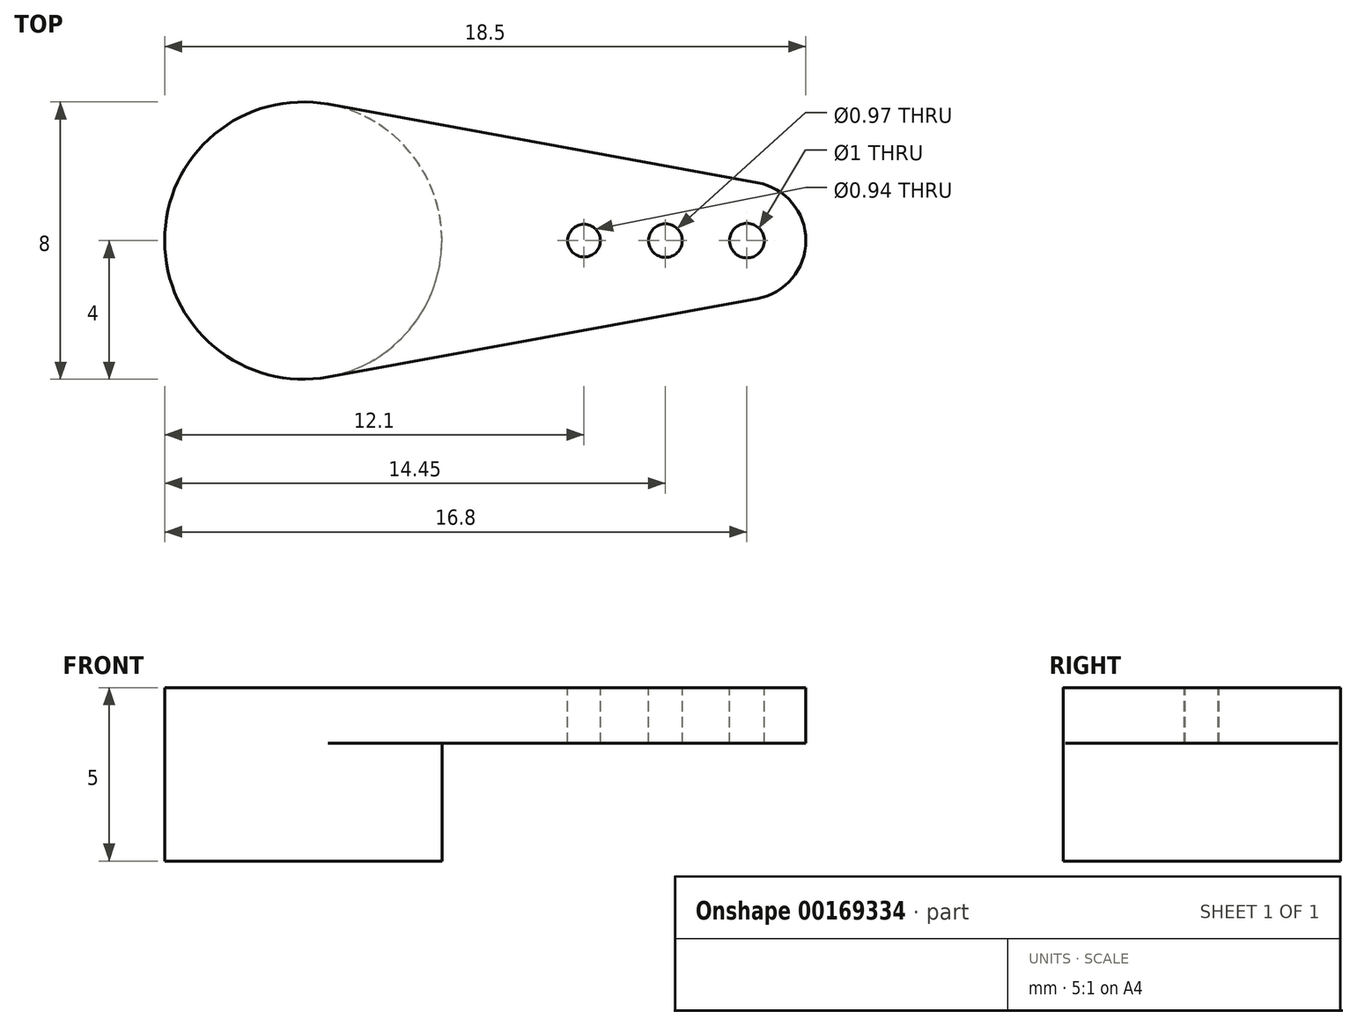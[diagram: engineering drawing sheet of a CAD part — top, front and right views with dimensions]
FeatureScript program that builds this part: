
annotation { "Feature Type Name" : "Feature", "Feature Type Description" : "" }
export const myFeature = defineFeature(function(context is Context, id is Id, definition is map)
    precondition{}
    {
        {
            var Q0;
            Q0=qCreatedBy(makeId("Front.planeOp"),FACE);
            var sketch = newSketch(context, id + "F0", { "sketchPlane" : qUnion([Q0])});
            skLineSegment(sketch, "E0.bottom", {"start": v(0, 0) * mm, "end": v(4, 0) * mm});
            skLineSegment(sketch, "E0.top", {"start": v(0, 3.4) * mm, "end": v(4, 3.4) * mm});
            skLineSegment(sketch, "E0.left", {"start": v(0, 0) * mm, "end": v(0, 3.4) * mm});
            skLineSegment(sketch, "E0.right", {"start": v(4, 0) * mm, "end": v(4, 3.4) * mm});
            skLineSegment(sketch, "E1.bottom", {"start": v(-4, 3.4) * mm, "end": v(14.5, 3.4) * mm});
            skLineSegment(sketch, "E1.top", {"start": v(-4, 5) * mm, "end": v(14.5, 5) * mm});
            skLineSegment(sketch, "E1.left", {"start": v(-4, 3.4) * mm, "end": v(-4, 5) * mm});
            skLineSegment(sketch, "E1.right", {"start": v(14.5, 3.4) * mm, "end": v(14.5, 5) * mm});
            skSolve(sketch);
        }
        {
            var Q0;
            {var subQ1=sQuery(id+"F0.wireOp",EDGE,"E0.bottom");Q0=makeQuery(id+"F0.imprint","IMPRINT",FACE,{"disambiguationData":[TD([[makeQuery(id+"F0.imprint","IMPRINT",EDGE,{"derivedFrom":subQ1}),1.0]])]});}
            var Q1;
            Q1=sQuery(id+"F0.wireOp",EDGE,"E0.left");
            revolve(context, id + "F1", {"entities" : qUnion([Q0]), "axis" : qUnion([Q1]), "revolveType" : RevolveType.FULL});
        }
        {
            var Q0;
            Q0=makeQuery(id+"F0.imprint","IMPRINT",FACE,{"disambiguationData":[TD([[makeQuery(id+"F0.imprint","IMPRINT",EDGE,{"derivedFrom":sQuery(id+"F0.wireOp",EDGE,"E1.top")}),-1.0]])]});
            extrude(context, id + "F2", {"entities" : qUnion([Q0]), "operationType" : NewBodyOperationType.ADD, "endBound" : BoundingType.SYMMETRIC, "depth" : 8 * mm});
        }
        {
            var Q0;
            Q0=makeQuery(id+"F2.opExtrude","SWEPT_FACE",FACE,{"disambiguationData":[OSD([sQuery(id+"F0.wireOp",EDGE,"E1.top")])]});
            var sketch = newSketch(context, id + "F3", { "sketchPlane" : qUnion([Q0])});
            skCircle(sketch, "E2", {"center": v(0, 0) * mm, "radius": 4 * mm});
            skCircle(sketch, "E3", {"center": v(12.8, 0) * mm, "radius": 1.7 * mm});
            skLineSegment(sketch, "E4", {"start": v(0.72, -3.93) * mm, "end": v(13.1, -1.67) * mm});
            skLineSegment(sketch, "E5", {"start": v(13.1, 1.67) * mm, "end": v(0.72, 3.93) * mm});
            skCircle(sketch, "E6", {"center": v(12.8, 0) * mm, "radius": 0.5 * mm});
            skCircle(sketch, "E7", {"center": v(10.45, 0) * mm, "radius": 0.49 * mm});
            skCircle(sketch, "E8", {"center": v(8.1, 0) * mm, "radius": 0.47 * mm});
            skSolve(sketch);
        }
        {
            var Q0;
            {var subQ6=sQuery(id+"F3.wireOp",EDGE,"E4");Q0=makeQuery(id+"F3.imprint","IMPRINT",FACE,{"disambiguationData":[TD([[makeQuery(id+"F3.imprint","IMPRINT",EDGE,{"derivedFrom":subQ6}),-1.0]])]});}
            var Q1;
            {var subQ0=sQuery(id+"F3.wireOp",EDGE,"E5");Q1=makeQuery(id+"F3.imprint","IMPRINT",FACE,{"disambiguationData":[TD([[makeQuery(id+"F3.imprint","IMPRINT",EDGE,{"derivedFrom":subQ0}),-1.0]])]});}
            var Q2;
            {var subQ0=sQuery(id+"F3.wireOp",EDGE,"E2");var subQ1=sQuery(id+"F0.wireOp",EDGE,"E1.top");var subQ2=makeQuery(id+"F2.opExtrude","CAP_EDGE",EDGE,{"disambiguationData":[OSD([subQ1])],"isStart":true});var subQ3=makeQuery(id+"F3.imprint","INTERSECT",VERTEX,{"derivedFrom":[subQ2,subQ0]});Q2=makeQuery(id+"F3.imprint","IMPRINT",FACE,{"disambiguationData":[TD([[makeQuery(id+"F3.imprint","IMPRINT",EDGE,{"disambiguationData":[TD([[subQ3,-1.0]])],"derivedFrom":subQ0}),-1.0]])]});}
            var Q3;
            {var subQ0=sQuery(id+"F3.wireOp",EDGE,"E2");var subQ1=sQuery(id+"F0.wireOp",EDGE,"E1.top");var subQ4=makeQuery(id+"F2.opExtrude","CAP_EDGE",EDGE,{"disambiguationData":[OSD([subQ1])],"isStart":false});var subQ5=makeQuery(id+"F3.imprint","INTERSECT",VERTEX,{"derivedFrom":[subQ4,subQ0]});Q3=makeQuery(id+"F3.imprint","IMPRINT",FACE,{"disambiguationData":[TD([[makeQuery(id+"F3.imprint","IMPRINT",EDGE,{"disambiguationData":[TD([[subQ5,1.0]])],"derivedFrom":subQ0}),-1.0]])]});}
            extrude(context, id + "F4", {"entities" : qUnion([Q0, Q1, Q2, Q3]), "operationType" : NewBodyOperationType.REMOVE, "oppositeDirection" : true, "depth" : 25 * mm});
        }
        {
            var Q0;
            Q0=makeQuery(id+"F3.imprint","IMPRINT",FACE,{"disambiguationData":[TD([[makeQuery(id+"F3.imprint","IMPRINT",EDGE,{"derivedFrom":sQuery(id+"F3.wireOp",EDGE,"E8")}),1.0]])]});
            var Q1;
            Q1=makeQuery(id+"F3.imprint","IMPRINT",FACE,{"disambiguationData":[TD([[makeQuery(id+"F3.imprint","IMPRINT",EDGE,{"derivedFrom":sQuery(id+"F3.wireOp",EDGE,"E6")}),1.0]])]});
            var Q2;
            Q2=makeQuery(id+"F3.imprint","IMPRINT",FACE,{"disambiguationData":[TD([[makeQuery(id+"F3.imprint","IMPRINT",EDGE,{"derivedFrom":sQuery(id+"F3.wireOp",EDGE,"E7")}),1.0]])]});
            extrude(context, id + "F5", {"entities" : qUnion([Q0, Q1, Q2]), "operationType" : NewBodyOperationType.REMOVE, "oppositeDirection" : true, "depth" : 25 * mm});
        }
    });
